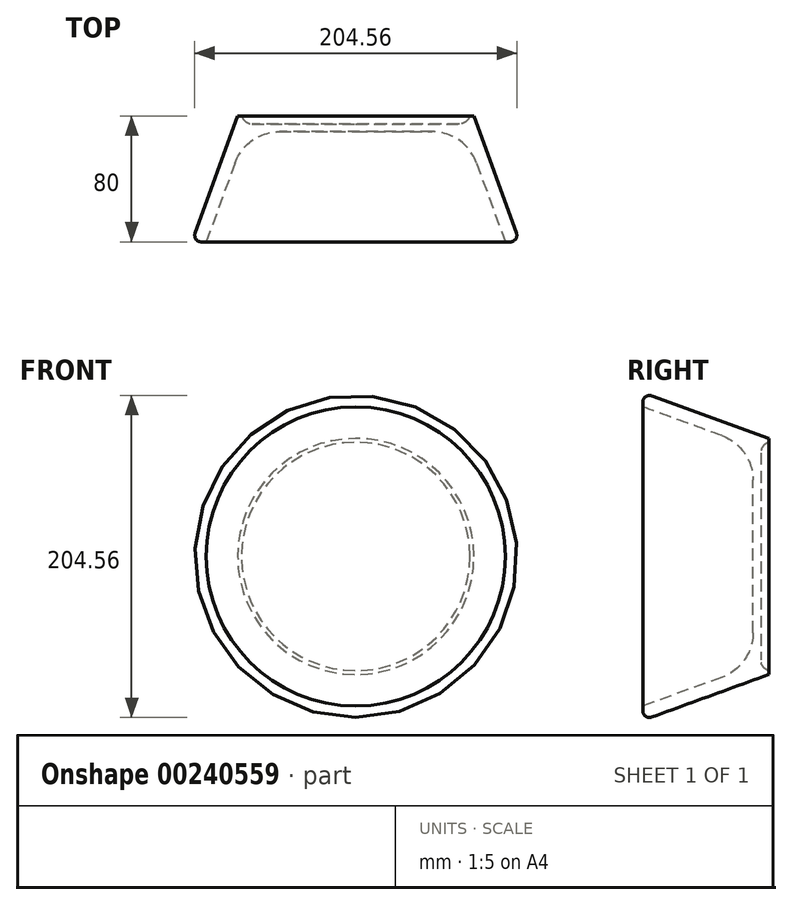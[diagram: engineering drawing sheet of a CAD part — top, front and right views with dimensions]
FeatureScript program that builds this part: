
annotation { "Feature Type Name" : "Feature", "Feature Type Description" : "" }
export const myFeature = defineFeature(function(context is Context, id is Id, definition is map)
    precondition{}
    {
        {
            var Q0;
            Q0=qCreatedBy(makeId("Front.planeOp"),FACE);
            var sketch = newSketch(context, id + "F0", { "sketchPlane" : qUnion([Q0])});
            skCircle(sketch, "E0", {"center": v(0, 0) * mm, "radius": 75 * mm});
            skSolve(sketch);
        }
        {
            var Q0;
            Q0=makeQuery(id+"F0.imprint","IMPRINT",FACE,{"disambiguationData":[TD([[makeQuery(id+"F0.imprint","IMPRINT",EDGE,{"derivedFrom":sQuery(id+"F0.wireOp",EDGE,"E0")}),1.0]])]});
            extrude(context, id + "F1", {"entities" : qUnion([Q0]), "depth" : 80 * mm, "hasDraft" : true, "draftAngle" : 20 * degree});
        }
        {
            var Q0;
            Q0=makeQuery(id+"F1.opExtrude","CAP_FACE",FACE,{"disambiguationData":[OSD([sQuery(id+"F0.wireOp",EDGE,"E0")])],"isStart":false});
            var sketch = newSketch(context, id + "F2", { "sketchPlane" : qUnion([Q0])});
            skCircle(sketch, "E1", {"center": v(0, 0) * mm, "radius": 95 * mm});
            skSolve(sketch);
        }
        {
            var Q0;
            Q0=makeQuery(id+"F2.imprint","IMPRINT",FACE,{"disambiguationData":[TD([[makeQuery(id+"F2.imprint","IMPRINT",EDGE,{"derivedFrom":sQuery(id+"F2.wireOp",EDGE,"E1")}),1.0]])]});
            extrude(context, id + "F3", {"entities" : qUnion([Q0]), "operationType" : NewBodyOperationType.REMOVE, "oppositeDirection" : true, "depth" : 70 * mm, "hasDraft" : true, "draftAngle" : 20 * degree, "draftPullDirection" : true});
        }
        {
            var Q0;
            Q0=makeQuery(id+"F3.boolean.opBoolean","COPY",EDGE,{"derivedFrom":makeQuery(id+"F3.opExtrude","CAP_EDGE",EDGE,{"disambiguationData":[OSD([sQuery(id+"F2.wireOp",EDGE,"E1")])],"isStart":false})});
            fillet(context, id + "F4", {"entities" : qUnion([Q0]), "radius" : 30 * mm, "tangentPropagation" : true, "allowEdgeOverflow" : false});
        }
        {
            var Q0;
            Q0=makeQuery(id+"F3.boolean.opBoolean","COPY",EDGE,{"derivedFrom":makeQuery(id+"F3.opExtrude","CAP_EDGE",EDGE,{"disambiguationData":[OSD([sQuery(id+"F2.wireOp",EDGE,"E1")])],"isStart":true})});
            var Q1;
            Q1=makeQuery(id+"F1.opExtrude","CAP_EDGE",EDGE,{"disambiguationData":[OSD([sQuery(id+"F0.wireOp",EDGE,"E0")])],"isStart":false});
            fillet(context, id + "F5", {"entities" : qUnion([Q0, Q1]), "radius" : 4.28 * mm, "tangentPropagation" : true, "allowEdgeOverflow" : false});
        }
        {
            var Q0;
            Q0=makeQuery(id+"F1.opExtrude","CAP_FACE",FACE,{"disambiguationData":[OSD([sQuery(id+"F0.wireOp",EDGE,"E0")])],"isStart":true});
            var sketch = newSketch(context, id + "F6", { "sketchPlane" : qUnion([Q0])});
            skCircle(sketch, "E2", {"center": v(0, 0) * mm, "radius": 72.5 * mm});
            skSolve(sketch);
        }
        {
            var Q0;
            Q0=makeQuery(id+"F6.imprint","IMPRINT",FACE,{"disambiguationData":[TD([[makeQuery(id+"F6.imprint","IMPRINT",EDGE,{"derivedFrom":sQuery(id+"F6.wireOp",EDGE,"E2")}),1.0]])]});
            extrude(context, id + "F7", {"entities" : qUnion([Q0]), "operationType" : NewBodyOperationType.REMOVE, "oppositeDirection" : true, "depth" : 5 * mm});
        }
        {
            var Q0;
            Q0=makeQuery(id+"F7.boolean.opBoolean","COPY",EDGE,{"derivedFrom":makeQuery(id+"F7.opExtrude","CAP_EDGE",EDGE,{"disambiguationData":[OSD([sQuery(id+"F6.wireOp",EDGE,"E2")])],"isStart":false})});
            fillet(context, id + "F8", {"entities" : qUnion([Q0]), "radius" : 7 * mm, "tangentPropagation" : true, "allowEdgeOverflow" : false});
        }
    });
